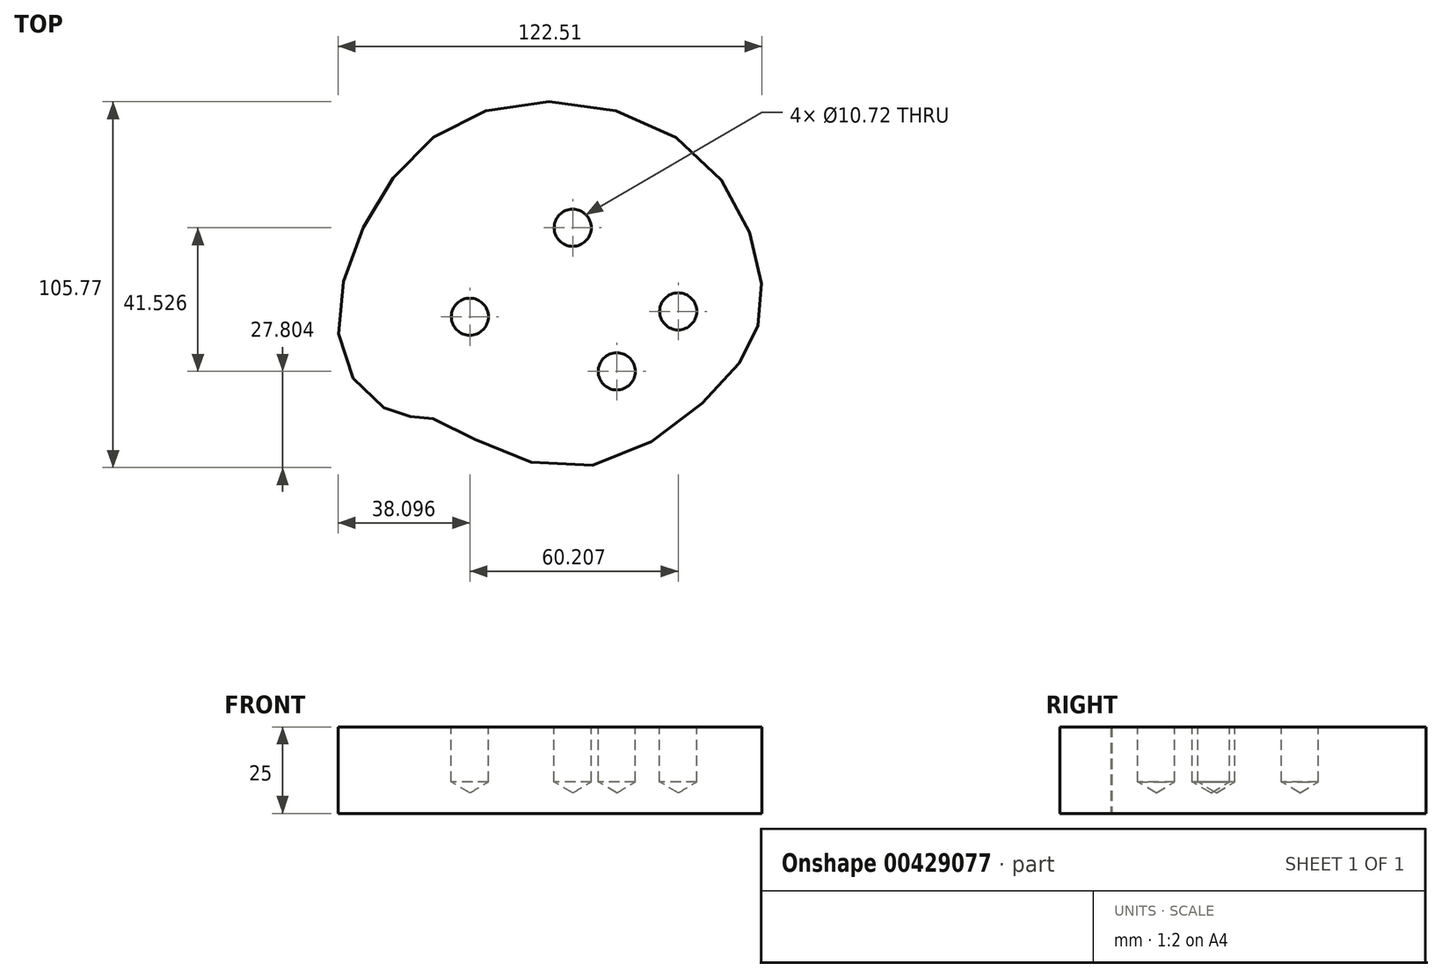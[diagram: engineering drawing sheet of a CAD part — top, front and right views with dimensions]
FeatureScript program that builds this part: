
annotation { "Feature Type Name" : "Feature", "Feature Type Description" : "" }
export const myFeature = defineFeature(function(context is Context, id is Id, definition is map)
    precondition{}
    {
        {
            var Q0;
            Q0=qCreatedBy(makeId("Top.planeOp"),FACE);
            var sketch = newSketch(context, id + "F0", { "sketchPlane" : qUnion([Q0])});
            skFitSpline(sketch, "E0", {"points": [v(-49.8, 0) * mm, v(-15.42, 33.57) * mm, v(44.35, 23.47) * mm, v(65.36, -18.01) * mm, v(55.8, -42.85) * mm, v(8.32, -69.32) * mm, v(-31.52, -54.58) * mm, v(-38.16, -54.54) * mm, v(-54.72, -39.84) * mm, v(-49.8, 0) * mm]});
            skSolve(sketch);
        }
        {
            var Q0;
            Q0=makeQuery(id+"F0.imprint","IMPRINT",FACE,{"disambiguationData":[TD([[makeQuery(id+"F0.imprint","IMPRINT",EDGE,{"derivedFrom":sQuery(id+"F0.wireOp",EDGE,"E0")}),-1.0]])]});
            extrude(context, id + "F1", {"entities" : qUnion([Q0]), "depth" : 25 * mm});
        }
        {
            var Q0;
            Q0=makeQuery(id+"F1.opExtrude","CAP_FACE",FACE,{"disambiguationData":[OSD([sQuery(id+"F0.wireOp",EDGE,"E0")])],"isStart":false});
            var sketch = newSketch(context, id + "F2", { "sketchPlane" : qUnion([Q0])});
            skCircle(sketch, "E1", {"center": v(10.71, 0) * mm, "radius": 9.92 * mm});
            skCircle(sketch, "E2", {"center": v(-19, -25.7) * mm, "radius": 4.82 * mm});
            skCircle(sketch, "E3", {"center": v(23.45, -41.53) * mm, "radius": 6.3 * mm});
            skCircle(sketch, "E4", {"center": v(41.2, -24.16) * mm, "radius": 9.57 * mm});
            skSolve(sketch);
        }
        {
            var Q0;
            Q0=sQuery(id+"F2.wireOp",VERTEX,"E1.center");
            var Q1;
            Q1=sQuery(id+"F2.wireOp",VERTEX,"E2.center");
            var Q2;
            Q2=sQuery(id+"F2.wireOp",VERTEX,"E3.center");
            var Q3;
            Q3=sQuery(id+"F2.wireOp",VERTEX,"E4.center");
            var Q4;
            Q4=makeQuery(id+"F1.opExtrude","SWEPT_BODY",BODY,{"disambiguationData":[OSD([sQuery(id+"F0.wireOp",EDGE,"E0")])]});
            hole(context, id + "F3", {"style" : HoleStyle.SIMPLE, "endStyle" : HoleEndStyle.BLIND, "standardTappedOrClearance" : lookupTablePath({ "standard" : "ANSI", "engagement" : "75%", "pitch" : "13 tpi", "size" : "1/2", "type" : "Tapped" }), "standardBlindInLast" : lookupTablePath({ "standard" : "ANSI", "engagement" : "75%", "pitch" : "13 tpi", "size" : "1/2", "type" : "Tapped" }), "holeDiameter" : 10.72 * mm, "showTappedDepth" : true, "holeDepth" : 15.86 * mm, "isTappedThrough" : true, "tappedDepth" : 10 * mm, "tapClearance" : 3, "startFromSketch" : true, "locations" : qUnion([Q0, Q1, Q2, Q3]), "scope" : qUnion([Q4]), "majorDiameter" : 12.7 * mm});
        }
    });
